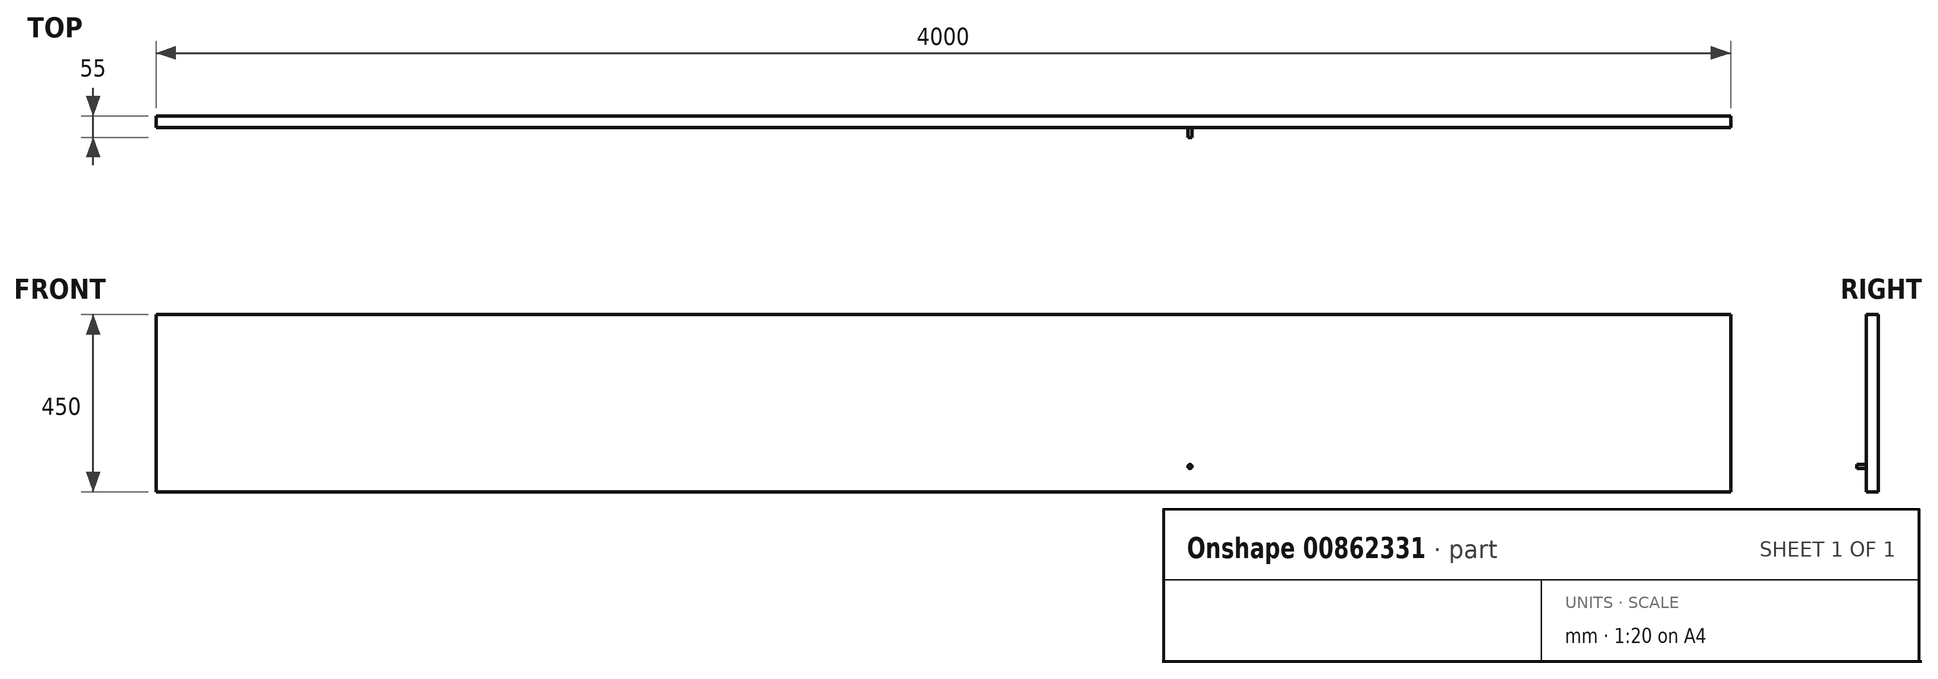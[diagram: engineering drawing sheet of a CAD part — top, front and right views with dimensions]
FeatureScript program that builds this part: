
annotation { "Feature Type Name" : "Feature", "Feature Type Description" : "" }
export const myFeature = defineFeature(function(context is Context, id is Id, definition is map)
    precondition{}
    {
        {
            var Q0;
            Q0=qCreatedBy(makeId("Front.planeOp"),FACE);
            var sketch = newSketch(context, id + "F0", { "sketchPlane" : qUnion([Q0])});
            skLineSegment(sketch, "E0.bottom", {"start": v(0, 0) * mm, "end": v(-4000, 0) * mm});
            skLineSegment(sketch, "E0.top", {"start": v(0, 450) * mm, "end": v(-4000, 450) * mm});
            skLineSegment(sketch, "E0.left", {"start": v(0, 0) * mm, "end": v(0, 450) * mm});
            skLineSegment(sketch, "E0.right", {"start": v(-4000, 0) * mm, "end": v(-4000, 450) * mm});
            skLineSegment(sketch, "E1.left", {"start": v(-942.32, 306.92) * mm, "end": v(-942.32, 296.92) * mm});
            skLineSegment(sketch, "E1.right", {"start": v(857.68, 306.92) * mm, "end": v(857.68, 296.92) * mm});
            skSolve(sketch);
        }
        {
            var Q0;
            Q0 = qSketchRegion(id + "F0", true);
            extrude(context, id + "F1", {"entities" : qUnion([Q0]), "depth" : 30 * mm, "offsetDistance" : 25 * mm});
        }
        {
            var Q0;
            Q0=makeQuery(id+"F1.opExtrude","CAP_FACE",FACE,{"disambiguationData":[OSD([sQuery(id+"F0.wireOp",EDGE,"E0.bottom"),sQuery(id+"F0.wireOp",EDGE,"E0.top"),sQuery(id+"F0.wireOp",EDGE,"E0.left"),sQuery(id+"F0.wireOp",EDGE,"E0.right")])],"isStart":false});
            var sketch = newSketch(context, id + "F2", { "sketchPlane" : qUnion([Q0])});
            skCircle(sketch, "E2", {"center": v(-1373.42, 64.07) * mm, "radius": 5 * mm});
            skSolve(sketch);
        }
        {
            var Q0;
            Q0=makeQuery(id+"F2.imprint","IMPRINT",FACE,{"disambiguationData":[TD([[makeQuery(id+"F2.imprint","IMPRINT",EDGE,{"derivedFrom":sQuery(id+"F2.wireOp",EDGE,"E2")}),1.0]])]});
            extrude(context, id + "F3", {"entities" : qUnion([Q0]), "operationType" : NewBodyOperationType.ADD, "depth" : 25 * mm, "offsetDistance" : 25 * mm});
        }
    });
